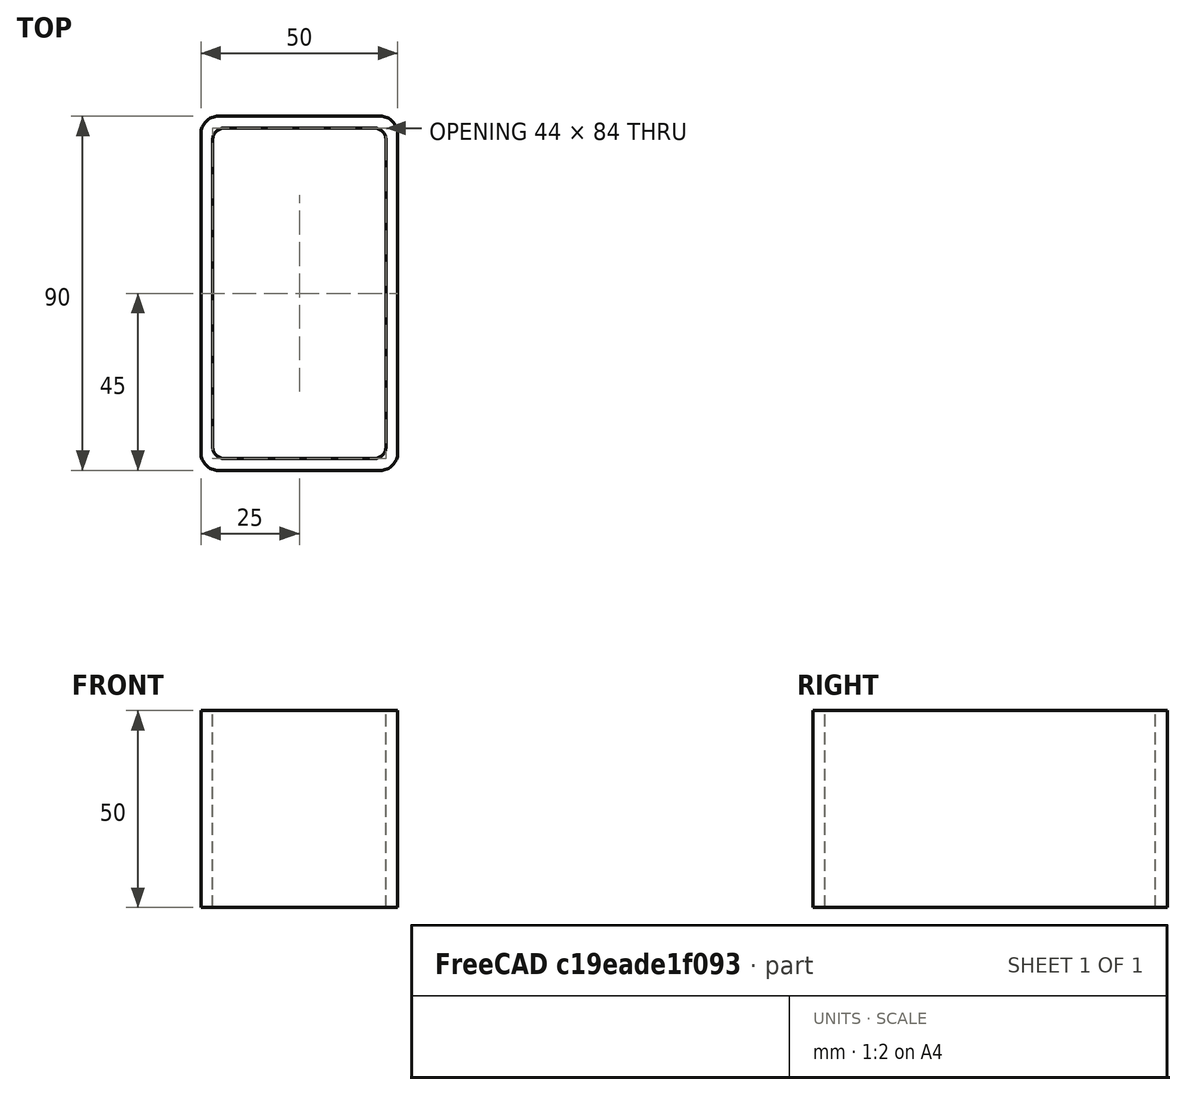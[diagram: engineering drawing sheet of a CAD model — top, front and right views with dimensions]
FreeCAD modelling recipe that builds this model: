
FCSTD DOCUMENT  (FreeCAD 0.15R4671 (Git))
Label: Rectangular hollow section 90x50x3 EN10219 S235JRH
License: All rights reserved
LicenseURL: http://en.wikipedia.org/wiki/All_rights_reserved
objects: Sketcher::SketchObject×1, Part::Extrusion×1
note: 2 computed .brp shape members not serialized (recipe doc carries the construction recipe); baked Part::Feature solids carry a one-line shape summary decoded from their .brp

FEATURE [Sketcher::SketchObject] Sketch
  sketch-geometry (16):
    g0: LineSegment StartX=-19 StartY=42 StartZ=0 EndX=19 EndY=42 EndZ=0
    g1: LineSegment StartX=22 StartY=39 StartZ=0 EndX=22 EndY=-39 EndZ=0
    g2: LineSegment StartX=19 StartY=-42 StartZ=0 EndX=-19 EndY=-42 EndZ=0
    g3: LineSegment StartX=-22 StartY=-39 StartZ=0 EndX=-22 EndY=39 EndZ=0
    g4: LineSegment StartX=-20.5 StartY=45 StartZ=0 EndX=20.5 EndY=45 EndZ=0
    g5: LineSegment StartX=25 StartY=40.5 StartZ=0 EndX=25 EndY=-40.5 EndZ=0
    g6: LineSegment StartX=20.5 StartY=-45 StartZ=0 EndX=-20.5 EndY=-45 EndZ=0
    g7: LineSegment StartX=-25 StartY=-40.5 StartZ=0 EndX=-25 EndY=40.5 EndZ=0
    g8: ArcOfCircle CenterX=-19 CenterY=39 CenterZ=0 NormalX=0 NormalY=0 NormalZ=1 Radius=3 StartAngle=1.5708 EndAngle=3.14159
    g9: ArcOfCircle CenterX=19 CenterY=39 CenterZ=0 NormalX=0 NormalY=0 NormalZ=1 Radius=3 StartAngle=0 EndAngle=1.5708
    g10: ArcOfCircle CenterX=19 CenterY=-39 CenterZ=0 NormalX=0 NormalY=0 NormalZ=1 Radius=3 StartAngle=4.71239 EndAngle=6.28319
    g11: ArcOfCircle CenterX=-19 CenterY=-39 CenterZ=0 NormalX=0 NormalY=0 NormalZ=1 Radius=3 StartAngle=3.14159 EndAngle=4.71239
    g12: ArcOfCircle CenterX=20.5 CenterY=40.5 CenterZ=0 NormalX=0 NormalY=0 NormalZ=1 Radius=4.5 StartAngle=0 EndAngle=1.5708
    g13: ArcOfCircle CenterX=20.5 CenterY=-40.5 CenterZ=0 NormalX=0 NormalY=0 NormalZ=1 Radius=4.5 StartAngle=4.71239 EndAngle=6.28319
    g14: ArcOfCircle CenterX=-20.5 CenterY=-40.5 CenterZ=0 NormalX=0 NormalY=0 NormalZ=1 Radius=4.5 StartAngle=3.14159 EndAngle=4.71239
    g15: ArcOfCircle CenterX=-20.5 CenterY=40.5 CenterZ=0 NormalX=0 NormalY=0 NormalZ=1 Radius=4.5 StartAngle=1.5708 EndAngle=3.14159
  constraints (36):
    c: Horizontal(g2)
    c: Vertical(g3)
    c: Horizontal(g6)
    c: Vertical(g7)
    c: Tangent(g3,g8) = 1.5708
    c: Tangent(g0,g8) = 1.5708
    c: Tangent(g0,g9) = 1.5708
    c: Tangent(g1,g9) = 1.5708
    c: Tangent(g1,g10) = 1.5708
    c: Tangent(g2,g10) = 1.5708
    c: Tangent(g2,g11) = 1.5708
    c: Tangent(g3,g11) = 1.5708
    c: Tangent(g4,g12) = 1.5708
    c: Tangent(g5,g12) = 1.5708
    c: Tangent(g5,g13) = 1.5708
    c: Tangent(g6,g13) = 1.5708
    c: Tangent(g6,g14) = 1.5708
    c: Tangent(g7,g14) = 1.5708
    c: Tangent(g7,g15) = 1.5708
    c: Tangent(g4,g15) = 1.5708
    c: Equal(g9,g8)
    c: Equal(g9,g11)
    c: Equal(g9,g10)
    c: Equal(g12,g15)
    c: Equal(g12,g14)
    c: Equal(g12,g13)
    c: Symmetric(g4,g6,g-1)
    c: Symmetric(g7,g5,g-2)
    c: DistanceY(g4,g6) = -90
    c: DistanceX(g7,g5) = 50
    c: Symmetric(g3,g1,g-2)
    c: Symmetric(g0,g2,g-1)
    c: DistanceY(g0,g4) = 3
    c: DistanceX(g5,g1) = -3
    c: Radius(g9) = 3
    c: Radius(g12) = 4.5
FEATURE [Part::Extrusion] Extrude  label="Rectangular hollow section 90x50x3 EN10219 S235JRH"
  Base = -> Sketch
  Dir = (0,0,50)
  Solid = true
